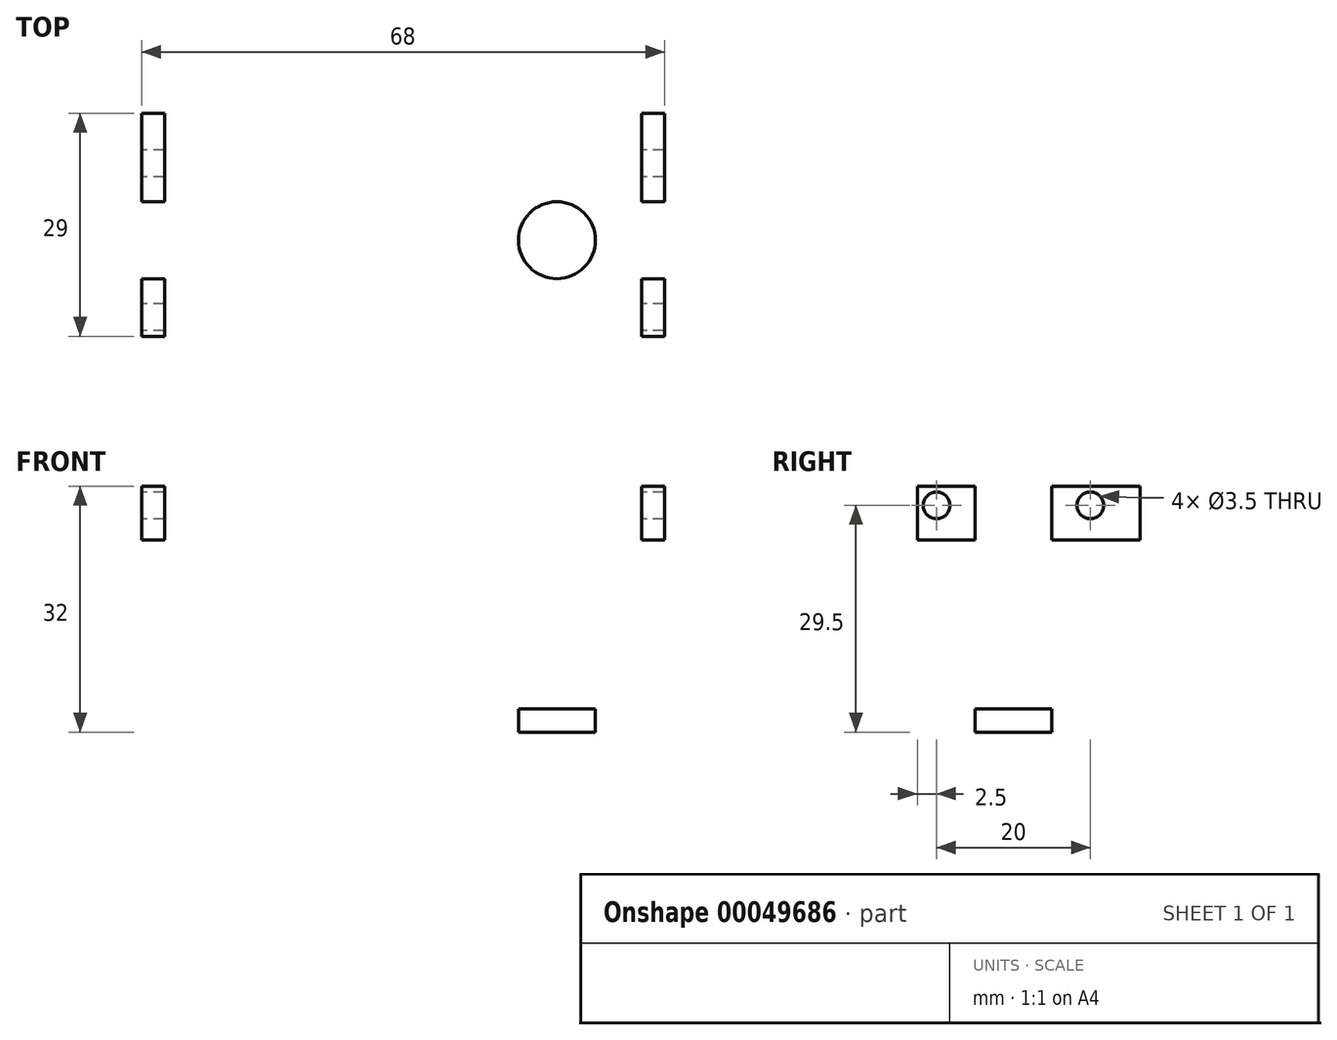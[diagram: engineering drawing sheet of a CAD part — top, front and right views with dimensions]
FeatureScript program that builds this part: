
annotation { "Feature Type Name" : "Feature", "Feature Type Description" : "" }
export const myFeature = defineFeature(function(context is Context, id is Id, definition is map)
    precondition{}
    {
        {
            var Q0;
            Q0=qCreatedBy(makeId("Top.planeOp"),FACE);
            var sketch = newSketch(context, id + "F0", { "sketchPlane" : qUnion([Q0])});
            skLineSegment(sketch, "E0.rect.bottom", {"start": v(34, 16.5) * mm, "end": v(-34, 16.5) * mm});
            skLineSegment(sketch, "E0.rect.top", {"start": v(34, -16.5) * mm, "end": v(-34, -16.5) * mm});
            skLineSegment(sketch, "E0.rect.left", {"start": v(34, 16.5) * mm, "end": v(34, -16.5) * mm});
            skLineSegment(sketch, "E0.rect.right", {"start": v(-34, 16.5) * mm, "end": v(-34, -16.5) * mm});
            skPoint(sketch, "E0.rect.middle", {"position": v(0, 0) * mm});
            skArc(sketch, "E1", {"start": v(-8, 16.5) * mm, "mid": v(0, 24.5) * mm, "end": v(8, 16.5) * mm});
            skLineSegment(sketch, "E2.bottom", {"start": v(-34, -16.5) * mm, "end": v(34, -16.5) * mm});
            skLineSegment(sketch, "E2.top", {"start": v(-34, -12.5) * mm, "end": v(34, -12.5) * mm});
            skLineSegment(sketch, "E2.left", {"start": v(-34, -16.5) * mm, "end": v(-34, -12.5) * mm});
            skLineSegment(sketch, "E2.right", {"start": v(34, -16.5) * mm, "end": v(34, -12.5) * mm});
            skLineSegment(sketch, "E3.bottom", {"start": v(-21, -12.5) * mm, "end": v(-9, -12.5) * mm});
            skLineSegment(sketch, "E3.top", {"start": v(-21, -14.5) * mm, "end": v(-9, -14.5) * mm});
            skLineSegment(sketch, "E3.left", {"start": v(-21, -12.5) * mm, "end": v(-21, -14.5) * mm});
            skLineSegment(sketch, "E3.right", {"start": v(-9, -12.5) * mm, "end": v(-9, -14.5) * mm});
            skLineSegment(sketch, "E4.MirrorCS", {"start": v(21, -12.5) * mm, "end": v(9, -12.5) * mm});
            skLineSegment(sketch, "E5.MirrorCS", {"start": v(9, -12.5) * mm, "end": v(9, -14.5) * mm});
            skLineSegment(sketch, "E6.MirrorCS", {"start": v(21, -14.5) * mm, "end": v(9, -14.5) * mm});
            skLineSegment(sketch, "E7.MirrorCS", {"start": v(21, -12.5) * mm, "end": v(21, -14.5) * mm});
            skSolve(sketch);
        }
        {
            var Q0;
            Q0=makeQuery(id+"F0.imprint","IMPRINT",FACE,{"disambiguationData":[TD([[makeQuery(id+"F0.imprint","IMPRINT",EDGE,{"derivedFrom":sQuery(id+"F0.wireOp",EDGE,"E0.rect.bottom")}),1.0]])]});
            var Q1;
            {var subQ0=sQuery(id+"F0.wireOp",EDGE,"E1");Q1=makeQuery(id+"F0.imprint","IMPRINT",FACE,{"disambiguationData":[TD([[makeQuery(id+"F0.imprint","IMPRINT",EDGE,{"derivedFrom":subQ0}),-1.0]])]});}
            var Q2;
            Q2=makeQuery(id+"F0.imprint","IMPRINT",FACE,{"disambiguationData":[TD([[makeQuery(id+"F0.imprint","IMPRINT",EDGE,{"derivedFrom":sQuery(id+"F0.wireOp",EDGE,"E3.bottom")}),-1.0]])]});
            var Q3;
            Q3=makeQuery(id+"F0.imprint","IMPRINT",FACE,{"disambiguationData":[TD([[makeQuery(id+"F0.imprint","IMPRINT",EDGE,{"derivedFrom":sQuery(id+"F0.wireOp",EDGE,"E4.MirrorCS")}),1.0]])]});
            extrude(context, id + "F1", {"entities" : qUnion([Q0, Q1, Q2, Q3]), "depth" : 3 * mm});
        }
        {
            var Q0;
            Q0=makeQuery(id+"F1.opExtrude","CAP_FACE",FACE,{"disambiguationData":[OSD([sQuery(id+"F0.wireOp",EDGE,"E0.rect.bottom"),sQuery(id+"F0.wireOp",EDGE,"E0.rect.top"),sQuery(id+"F0.wireOp",EDGE,"E0.rect.left"),sQuery(id+"F0.wireOp",EDGE,"E0.rect.right")])],"isStart":false});
            var sketch = newSketch(context, id + "F2", { "sketchPlane" : qUnion([Q0])});
            skLineSegment(sketch, "E8.bottom", {"start": v(-34, 16.5) * mm, "end": v(-31, 16.5) * mm});
            skLineSegment(sketch, "E8.top", {"start": v(-34, -12.5) * mm, "end": v(-31, -12.5) * mm});
            skLineSegment(sketch, "E8.left", {"start": v(-34, 16.5) * mm, "end": v(-34, -12.5) * mm});
            skLineSegment(sketch, "E8.right", {"start": v(-31, 16.5) * mm, "end": v(-31, -12.5) * mm});
            skLineSegment(sketch, "E9.MirrorCS", {"start": v(34, 16.5) * mm, "end": v(31, 16.5) * mm});
            skLineSegment(sketch, "E10.MirrorCS", {"start": v(34, -12.5) * mm, "end": v(31, -12.5) * mm});
            skLineSegment(sketch, "E11.MirrorCS", {"start": v(34, 16.5) * mm, "end": v(34, -12.5) * mm});
            skLineSegment(sketch, "E12.MirrorCS", {"start": v(31, 16.5) * mm, "end": v(31, -12.5) * mm});
            skSolve(sketch);
        }
        {
            var Q0;
            Q0=makeQuery(id+"F2.imprint","IMPRINT",FACE,{"disambiguationData":[TD([[makeQuery(id+"F2.imprint","IMPRINT",EDGE,{"derivedFrom":sQuery(id+"F2.wireOp",EDGE,"cdef8e28-4d2e-4085-974b-efc1f3721f57.bottom")}),1.0]])]});
            var Q1;
            Q1=makeQuery(id+"F2.imprint","IMPRINT",FACE,{"disambiguationData":[TD([[makeQuery(id+"F2.imprint","IMPRINT",EDGE,{"derivedFrom":sQuery(id+"F2.wireOp",EDGE,"2d693215-d6e5-4710-afa9-2f4ea4ccdc8b0.MirrorCS")}),1.0]])]});
            var Q2;
            Q2=makeQuery(id+"F2.imprint","IMPRINT",FACE,{"disambiguationData":[TD([[makeQuery(id+"F2.imprint","IMPRINT",EDGE,{"derivedFrom":sQuery(id+"F2.wireOp",EDGE,"E8.bottom")}),1.0]])]});
            var Q3;
            Q3=makeQuery(id+"F2.imprint","IMPRINT",FACE,{"disambiguationData":[TD([[makeQuery(id+"F2.imprint","IMPRINT",EDGE,{"derivedFrom":sQuery(id+"F2.wireOp",EDGE,"E9.MirrorCS")}),1.0]])]});
            extrude(context, id + "F3", {"entities" : qUnion([Q0, Q1, Q2, Q3]), "operationType" : NewBodyOperationType.ADD, "depth" : 29 * mm});
        }
        {
            var Q0;
            Q0=makeQuery(id+"F1.opExtrude","CAP_FACE",FACE,{"disambiguationData":[OSD([sQuery(id+"F0.wireOp",EDGE,"E0.rect.bottom"),sQuery(id+"F0.wireOp",EDGE,"E0.rect.top"),sQuery(id+"F0.wireOp",EDGE,"E0.rect.left"),sQuery(id+"F0.wireOp",EDGE,"E0.rect.right")])],"isStart":false});
            var sketch = newSketch(context, id + "F4", { "sketchPlane" : qUnion([Q0])});
            skLineSegment(sketch, "E13.bottom", {"start": v(-31, 16.5) * mm, "end": v(-16, 16.5) * mm});
            skLineSegment(sketch, "E13.top", {"start": v(-31, 14.5) * mm, "end": v(-16, 14.5) * mm});
            skLineSegment(sketch, "E13.left", {"start": v(-31, 16.5) * mm, "end": v(-31, 14.5) * mm});
            skLineSegment(sketch, "E13.right", {"start": v(-16, 16.5) * mm, "end": v(-16, 14.5) * mm});
            skLineSegment(sketch, "E14.MirrorCS", {"start": v(31, 16.5) * mm, "end": v(16, 16.5) * mm});
            skLineSegment(sketch, "E15.MirrorCS", {"start": v(31, 14.5) * mm, "end": v(16, 14.5) * mm});
            skLineSegment(sketch, "E16.MirrorCS", {"start": v(31, 16.5) * mm, "end": v(31, 14.5) * mm});
            skLineSegment(sketch, "E17.MirrorCS", {"start": v(16, 16.5) * mm, "end": v(16, 14.5) * mm});
            skSolve(sketch);
        }
        {
            var Q0;
            Q0=makeQuery(id+"F4.imprint","IMPRINT",FACE,{"disambiguationData":[TD([[makeQuery(id+"F4.imprint","IMPRINT",EDGE,{"derivedFrom":sQuery(id+"F4.wireOp",EDGE,"E13.bottom")}),1.0]])]});
            var Q1;
            Q1=makeQuery(id+"F4.imprint","IMPRINT",FACE,{"disambiguationData":[TD([[makeQuery(id+"F4.imprint","IMPRINT",EDGE,{"derivedFrom":sQuery(id+"F4.wireOp",EDGE,"E14.MirrorCS")}),1.0]])]});
            extrude(context, id + "F5", {"entities" : qUnion([Q0, Q1]), "operationType" : NewBodyOperationType.ADD, "depth" : 15 * mm});
        }
        {
            var Q0;
            Q0=makeQuery(id+"F5.opExtrude","CAP_EDGE",EDGE,{"disambiguationData":[OSD([sQuery(id+"F4.wireOp",EDGE,"E13.right")])],"isStart":false});
            var Q1;
            Q1=makeQuery(id+"F5.opExtrude","CAP_EDGE",EDGE,{"disambiguationData":[OSD([sQuery(id+"F4.wireOp",EDGE,"E17.MirrorCS")])],"isStart":false});
            chamfer(context, id + "F6", {"entities" : qUnion([Q0, Q1]), "width" : 15 * mm, "tangentPropagation" : true});
        }
        {
            var Q0;
            Q0=makeQuery(id+"F3.boolean.opBoolean","MERGE",FACE,{"derivedFrom":[makeQuery(id+"F1.opExtrude","SWEPT_FACE",FACE,{"disambiguationData":[OSD([sQuery(id+"F0.wireOp",EDGE,"E0.rect.right")])]}),makeQuery(id+"F3.opExtrude","SWEPT_FACE",FACE,{"disambiguationData":[OSD([sQuery(id+"F2.wireOp",EDGE,"cdef8e28-4d2e-4085-974b-efc1f3721f57.left")])]})]});
            var sketch = newSketch(context, id + "F7", { "sketchPlane" : qUnion([Q0])});
            skPoint(sketch, "E18", {"position": v(-10, 29.5) * mm});
            skPoint(sketch, "E19", {"position": v(-10, 9.5) * mm});
            skPoint(sketch, "E20.MirrorP", {"position": v(10, 9.5) * mm});
            skPoint(sketch, "E21.MirrorP", {"position": v(10, 29.5) * mm});
            skSolve(sketch);
        }
        {
            var Q0;
            Q0=sQuery(id+"F7.wireOp",VERTEX,"E21.MirrorP");
            var Q1;
            Q1=sQuery(id+"F7.wireOp",VERTEX,"E20.MirrorP");
            var Q2;
            Q2=sQuery(id+"F7.wireOp",VERTEX,"E19");
            var Q3;
            Q3=sQuery(id+"F7.wireOp",VERTEX,"E18");
            var Q4;
            Q4=makeQuery(id+"F1.opExtrude","SWEPT_BODY",BODY,{"disambiguationData":[OSD([sQuery(id+"F0.wireOp",EDGE,"E0.rect.bottom"),sQuery(id+"F0.wireOp",EDGE,"E0.rect.top"),sQuery(id+"F0.wireOp",EDGE,"E0.rect.left"),sQuery(id+"F0.wireOp",EDGE,"E0.rect.right")])]});
            hole(context, id + "F8", {"style" : HoleStyle.SIMPLE, "holeDiameter" : 3.5 * mm, "endStyle" : HoleEndStyle.THROUGH, "locations" : qUnion([Q0, Q1, Q2, Q3]), "scope" : qUnion([Q4])});
        }
        {
            var Q0;
            Q0=makeQuery(id+"F1.opExtrude","CAP_FACE",FACE,{"disambiguationData":[OSD([sQuery(id+"F0.wireOp",EDGE,"E0.rect.bottom"),sQuery(id+"F0.wireOp",EDGE,"E0.rect.top"),sQuery(id+"F0.wireOp",EDGE,"E0.rect.left"),sQuery(id+"F0.wireOp",EDGE,"E0.rect.right"),sQuery(id+"F0.wireOp",EDGE,"E1")])],"isStart":false});
            var sketch = newSketch(context, id + "F9", { "sketchPlane" : qUnion([Q0])});
            skCircle(sketch, "E22", {"center": v(0, 0) * mm, "radius": 18 * mm, "construction": true});
            skLineSegment(sketch, "E23", {"start": v(0, 0) * mm, "end": v(-15.59, -9) * mm, "construction": true});
            skLineSegment(sketch, "E24.MirrorCS", {"start": v(0, 0) * mm, "end": v(15.59, -9) * mm, "construction": true});
            skPoint(sketch, "E25", {"position": v(0, 18) * mm});
            skPoint(sketch, "E26", {"position": v(-15.59, -9) * mm});
            skPoint(sketch, "E27", {"position": v(15.59, -9) * mm});
            skSolve(sketch);
        }
        {
            var Q0;
            Q0=sQuery(id+"F9.wireOp",VERTEX,"E25");
            var Q1;
            Q1=sQuery(id+"F9.wireOp",VERTEX,"E26");
            var Q2;
            Q2=sQuery(id+"F9.wireOp",VERTEX,"E27");
            var Q3;
            Q3=makeQuery(id+"F1.opExtrude","SWEPT_BODY",BODY,{"disambiguationData":[OSD([sQuery(id+"F0.wireOp",EDGE,"E0.rect.bottom"),sQuery(id+"F0.wireOp",EDGE,"E0.rect.top"),sQuery(id+"F0.wireOp",EDGE,"E0.rect.left"),sQuery(id+"F0.wireOp",EDGE,"E0.rect.right"),sQuery(id+"F0.wireOp",EDGE,"E1")])]});
            hole(context, id + "F10", {"style" : HoleStyle.C_SINK, "holeDiameter" : 3.5 * mm, "cSinkDiameter" : 7 * mm, "endStyle" : HoleEndStyle.THROUGH, "locations" : qUnion([Q0, Q1, Q2]), "scope" : qUnion([Q3]), "cSinkAngle" : 90 * degree});
        }
        {
            var Q0;
            Q0=makeQuery(id+"F1.opExtrude","CAP_FACE",FACE,{"disambiguationData":[OSD([sQuery(id+"F0.wireOp",EDGE,"E0.rect.bottom"),sQuery(id+"F0.wireOp",EDGE,"E0.rect.top"),sQuery(id+"F0.wireOp",EDGE,"E0.rect.left"),sQuery(id+"F0.wireOp",EDGE,"E0.rect.right"),sQuery(id+"F0.wireOp",EDGE,"E1")])],"isStart":true});
            var sketch = newSketch(context, id + "F11", { "sketchPlane" : qUnion([Q0])});
            skCircle(sketch, "E28", {"center": v(0, 0) * mm, "radius": 7.5 * mm});
            skCircle(sketch, "E29", {"center": v(-20, 0) * mm, "radius": 5 * mm});
            skCircle(sketch, "E30.MirrorC", {"center": v(20, 0) * mm, "radius": 5 * mm});
            skSolve(sketch);
        }
        {
            var Q0;
            Q0=makeQuery(id+"F11.imprint","IMPRINT",FACE,{"disambiguationData":[TD([[makeQuery(id+"F11.imprint","IMPRINT",EDGE,{"derivedFrom":sQuery(id+"F11.wireOp",EDGE,"E28")}),1.0]])]});
            var Q1;
            Q1=makeQuery(id+"F11.imprint","IMPRINT",FACE,{"disambiguationData":[TD([[makeQuery(id+"F11.imprint","IMPRINT",EDGE,{"derivedFrom":sQuery(id+"F11.wireOp",EDGE,"E30.MirrorC")}),-1.0]])]});
            var Q2;
            Q2=makeQuery(id+"F11.imprint","IMPRINT",FACE,{"disambiguationData":[TD([[makeQuery(id+"F11.imprint","IMPRINT",EDGE,{"derivedFrom":sQuery(id+"F11.wireOp",EDGE,"E29")}),1.0]])]});
            extrude(context, id + "F12", {"entities" : qUnion([Q0, Q1, Q2]), "operationType" : NewBodyOperationType.REMOVE, "oppositeDirection" : true, "depth" : 25 * mm});
        }
        {
            var Q0;
            Q0=makeQuery(id+"F3.boolean.opBoolean","MERGE",FACE,{"derivedFrom":[makeQuery(id+"F1.opExtrude","SWEPT_FACE",FACE,{"disambiguationData":[OSD([sQuery(id+"F0.wireOp",EDGE,"E0.rect.left")])]}),makeQuery(id+"F3.opExtrude","SWEPT_FACE",FACE,{"disambiguationData":[OSD([sQuery(id+"F2.wireOp",EDGE,"2d693215-d6e5-4710-afa9-2f4ea4ccdc8b1.MirrorCS")])]})]});
            var sketch = newSketch(context, id + "F13", { "sketchPlane" : qUnion([Q0])});
            skLineSegment(sketch, "E31.rect.bottom", {"start": v(5, 32) * mm, "end": v(-5, 32) * mm});
            skLineSegment(sketch, "E31.rect.top", {"start": v(5, 20) * mm, "end": v(-5, 20) * mm});
            skLineSegment(sketch, "E31.rect.left", {"start": v(5, 32) * mm, "end": v(5, 20) * mm});
            skLineSegment(sketch, "E31.rect.right", {"start": v(-5, 32) * mm, "end": v(-5, 20) * mm});
            skPoint(sketch, "E31.rect.middle", {"position": v(0, 26) * mm});
            skArc(sketch, "E32", {"start": v(-5, 20) * mm, "mid": v(0, 15) * mm, "end": v(5, 20) * mm});
            skSolve(sketch);
        }
        {
            var Q0;
            Q0=makeQuery(id+"F13.imprint","IMPRINT",FACE,{"disambiguationData":[TD([[makeQuery(id+"F13.imprint","IMPRINT",EDGE,{"derivedFrom":sQuery(id+"F13.wireOp",EDGE,"E31.rect.bottom")}),1.0]])]});
            var Q1;
            Q1=makeQuery(id+"F13.imprint","IMPRINT",FACE,{"disambiguationData":[TD([[makeQuery(id+"F13.imprint","IMPRINT",EDGE,{"derivedFrom":sQuery(id+"F13.wireOp",EDGE,"E31.rect.top")}),1.0]])]});
            extrude(context, id + "F14", {"entities" : qUnion([Q0, Q1]), "operationType" : NewBodyOperationType.REMOVE, "endBound" : BoundingType.THROUGH_ALL, "oppositeDirection" : true, "depth" : 25 * mm});
        }
    });
